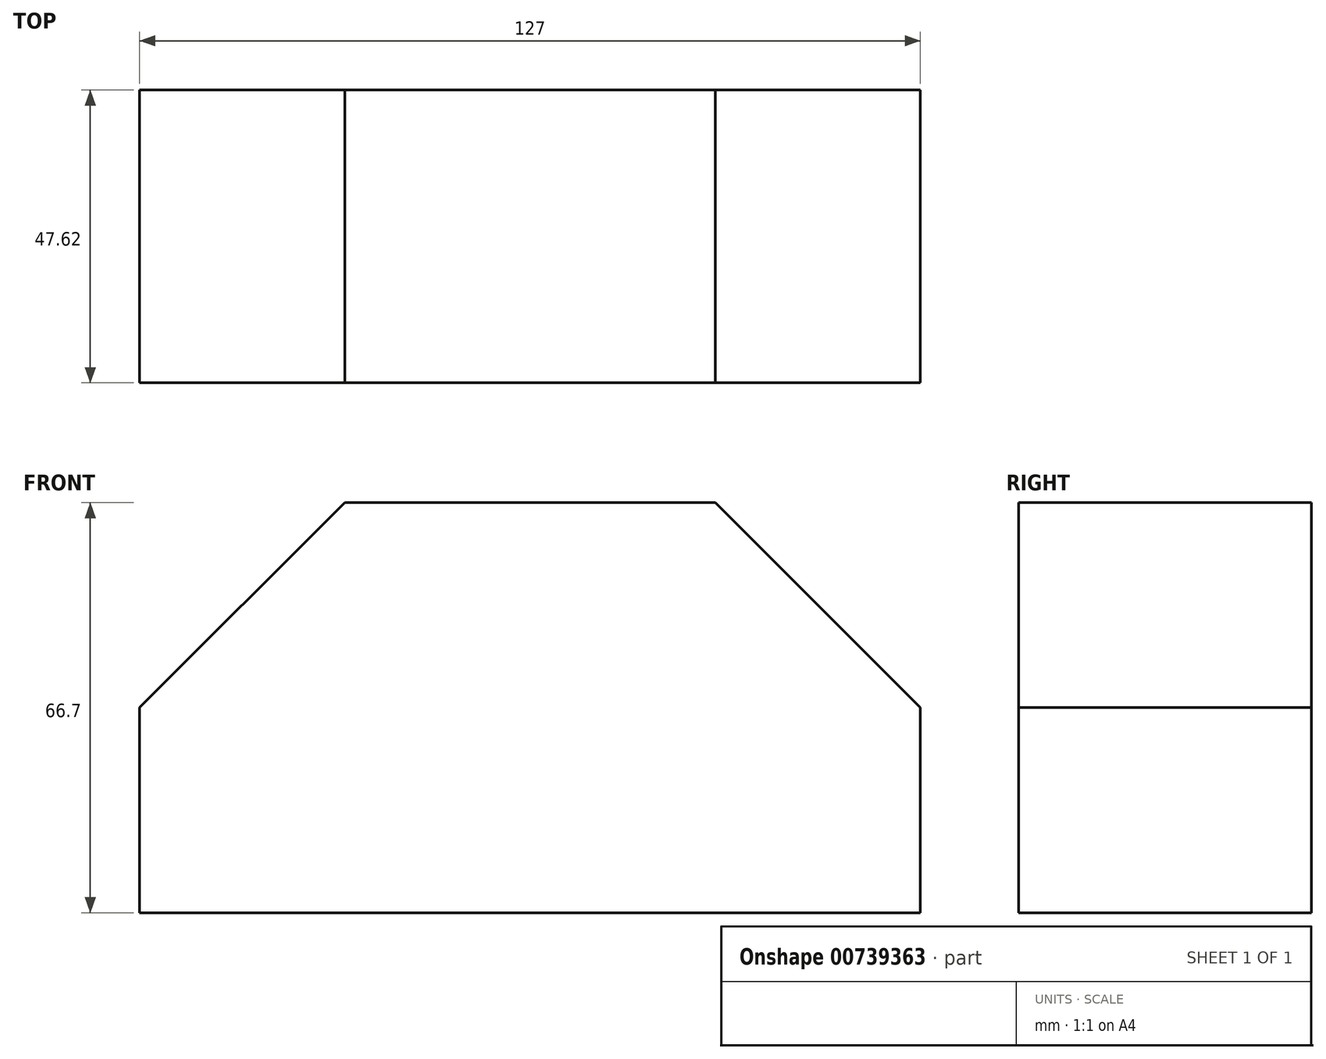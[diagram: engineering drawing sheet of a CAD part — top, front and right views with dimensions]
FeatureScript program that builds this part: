
annotation { "Feature Type Name" : "Feature", "Feature Type Description" : "" }
export const myFeature = defineFeature(function(context is Context, id is Id, definition is map)
    precondition{}
    {
        {
            var Q0;
            Q0=qCreatedBy(makeId("Front.planeOp"),FACE);
            var sketch = newSketch(context, id + "F0", { "sketchPlane" : qUnion([Q0])});
            skLineSegment(sketch, "E0", {"start": v(0, 0) * mm, "end": v(127, 0) * mm});
            skLineSegment(sketch, "E1", {"start": v(127, 0) * mm, "end": v(127, 33.35) * mm});
            skLineSegment(sketch, "E2", {"start": v(0, 0) * mm, "end": v(0, 33.35) * mm});
            skLineSegment(sketch, "E3", {"start": v(33.35, 66.7) * mm, "end": v(93.65, 66.7) * mm});
            skLineSegment(sketch, "E4", {"start": v(-21.02, 0) * mm, "end": v(-21.02, 33.35) * mm});
            skLineSegment(sketch, "E5", {"start": v(0, 33.35) * mm, "end": v(33.35, 66.7) * mm});
            skLineSegment(sketch, "E6", {"start": v(154.4, 0) * mm, "end": v(154.4, 33.35) * mm});
            skLineSegment(sketch, "E7", {"start": v(127, 33.35) * mm, "end": v(93.65, 66.7) * mm});
            skPoint(sketch, "E8.orphan", {"position": v(127, 66.7) * mm});
            skPoint(sketch, "E9.end.orphan", {"position": v(93.65, 76.68) * mm});
            skPoint(sketch, "E9.start.orphan", {"position": v(127, 68.73) * mm});
            skPoint(sketch, "E10.end.orphan", {"position": v(33.35, 76.68) * mm});
            skPoint(sketch, "E10.start.orphan", {"position": v(0, 68.73) * mm});
            skSolve(sketch);
        }
        {
            var Q0;
            Q0=makeQuery(id+"F0.imprint","IMPRINT",FACE,{"disambiguationData":[TD([[makeQuery(id+"F0.imprint","IMPRINT",EDGE,{"derivedFrom":sQuery(id+"F0.wireOp",EDGE,"E0")}),1.0]])]});
            extrude(context, id + "F1", {"entities" : qUnion([Q0]), "depth" : 47.62 * mm, "offsetDistance" : 25.4 * mm});
        }
    });
